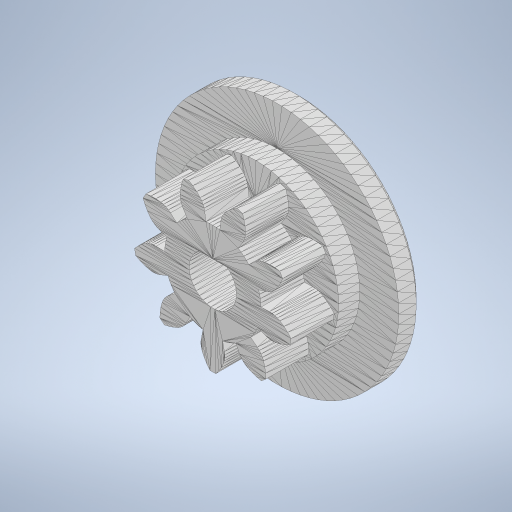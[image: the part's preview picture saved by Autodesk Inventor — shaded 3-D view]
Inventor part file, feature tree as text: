
AUTODESK INVENTOR PART (.ipt)
format: ipt  version: 2023.2 (Build 272271000, 271)  size: 290,816 bytes
history: native  units: mm
features: other x2, sketch x2, extrude x1, chamfer x1
ambient origin geometry x8: Origin, YZ Plane, XZ Plane, XY Plane, X Axis, Y Axis, Z Axis, Center Point
bodies: Body1 (feature_tree)
feature tree (6):
  other  "06-Gear"
  sketch  "Skizze2"  dims[d6=3.5mm d7=0.0mm d8=0.45mm d9=2.0mm d10=45.0deg]
  extrude  "Extrusion2"  Depth=3.5mm TaperAngle=45.0deg
  chamfer  "Fase2"  [1 undecoded]
  sketch  "Skizze3"
  other  "MeshFeature1"
note: 1 required parameter value undecoded (feature->parameter linkage not recoverable at this tier; creation-order binding heuristic only, values carry confidence <= 0.55)
